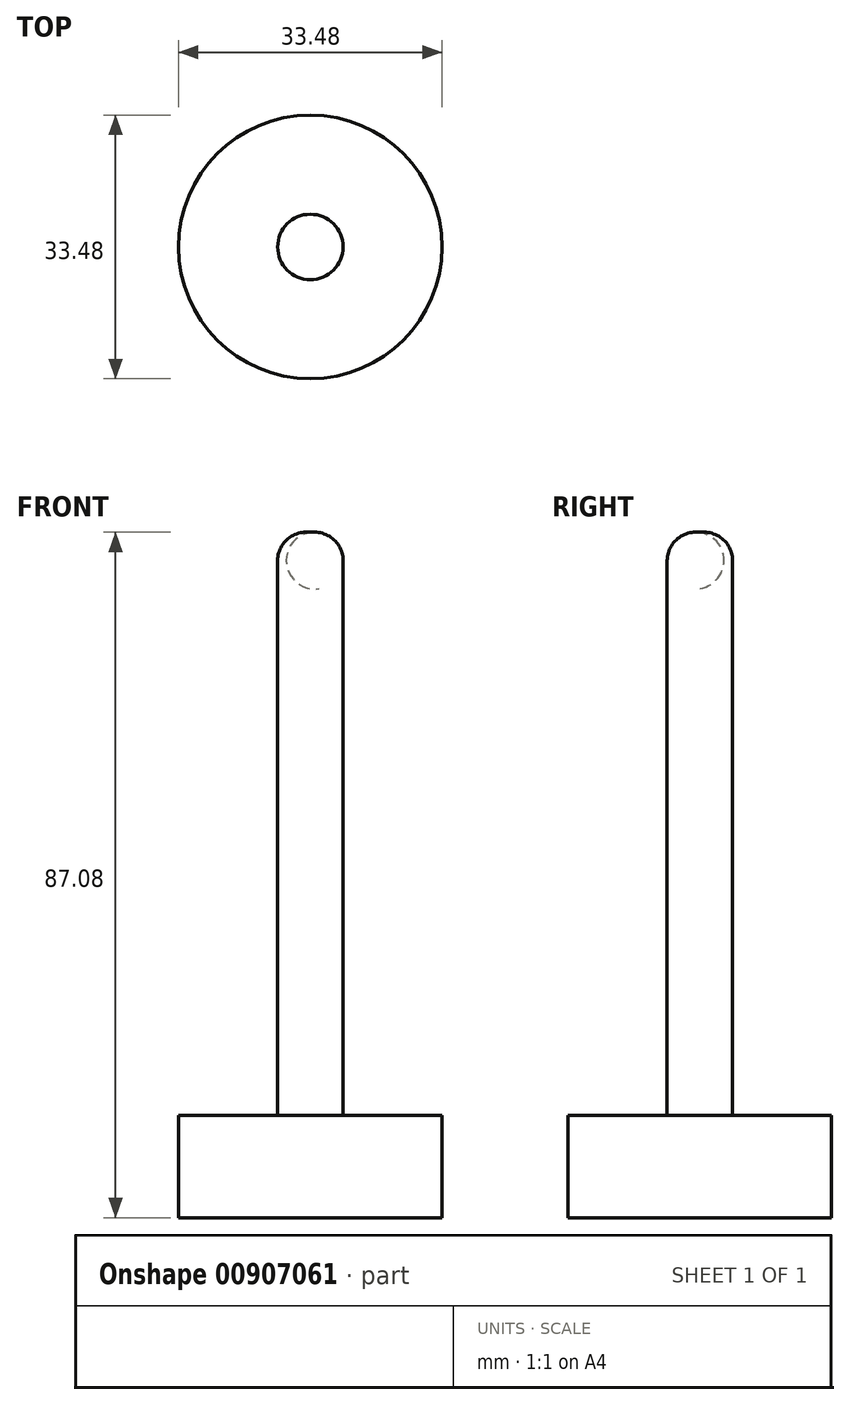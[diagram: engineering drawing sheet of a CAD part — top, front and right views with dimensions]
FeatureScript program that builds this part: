
annotation { "Feature Type Name" : "Feature", "Feature Type Description" : "" }
export const myFeature = defineFeature(function(context is Context, id is Id, definition is map)
    precondition{}
    {
        {
            var Q0;
            Q0=qCreatedBy(makeId("Front.planeOp"),FACE);
            var sketch = newSketch(context, id + "F0", { "sketchPlane" : qUnion([Q0])});
            skLineSegment(sketch, "E0", {"start": v(0, 67.43) * mm, "end": v(0, -19.6) * mm});
            skLineSegment(sketch, "E1", {"start": v(0, -19.6) * mm, "end": v(16.74, -19.6) * mm});
            skLineSegment(sketch, "E2", {"start": v(16.74, -19.6) * mm, "end": v(0, -19.6) * mm});
            skLineSegment(sketch, "E3", {"start": v(16.74, -19.6) * mm, "end": v(16.74, -6.6) * mm});
            skLineSegment(sketch, "E4", {"start": v(16.74, -6.6) * mm, "end": v(4.15, -6.6) * mm});
            skLineSegment(sketch, "E5", {"start": v(4.15, -6.6) * mm, "end": v(4.15, 63.87) * mm});
            skArc(sketch, "E6", {"start": v(4.15, 63.87) * mm, "mid": v(2.9, 66.6) * mm, "end": v(0, 67.43) * mm});
            skSolve(sketch);
        }
        {
            var Q0;
            Q0 = qSketchRegion(id + "F0", true);
            var Q1;
            Q1=sQuery(id+"F0.wireOp",EDGE,"E0");
            revolve(context, id + "F1", {"surfaceOperationType" : NewSurfaceOperationType.NEW, "entities" : qUnion([Q0]), "axis" : qUnion([Q1]), "revolveType" : RevolveType.FULL});
        }
    });
